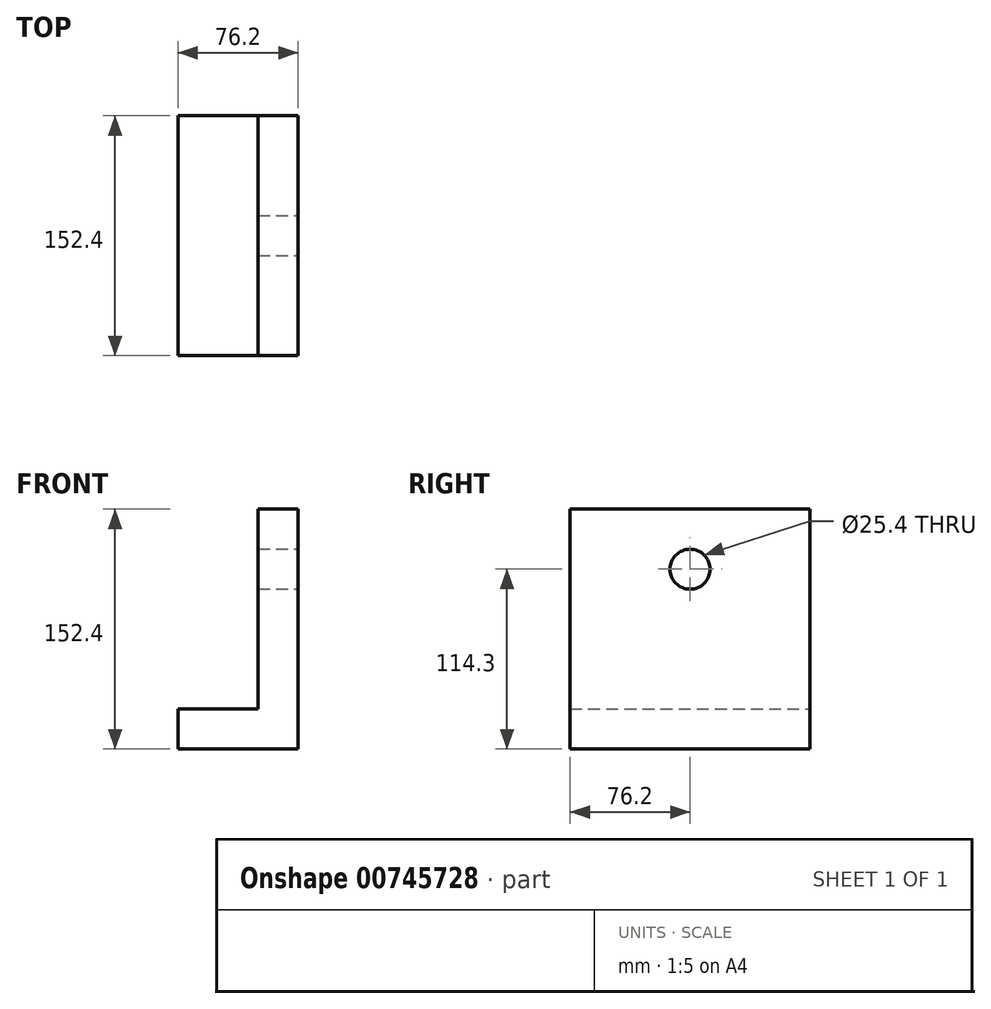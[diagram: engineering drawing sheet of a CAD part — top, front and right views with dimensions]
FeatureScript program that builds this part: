
annotation { "Feature Type Name" : "Feature", "Feature Type Description" : "" }
export const myFeature = defineFeature(function(context is Context, id is Id, definition is map)
    precondition{}
    {
        {
            var Q0;
            Q0=qCreatedBy(makeId("Front.planeOp"),FACE);
            var sketch = newSketch(context, id + "F0", { "sketchPlane" : qUnion([Q0])});
            skLineSegment(sketch, "E0", {"start": v(0, 0) * mm, "end": v(-76.2, 0) * mm});
            skLineSegment(sketch, "E1", {"start": v(-76.2, 0) * mm, "end": v(-76.2, 25.4) * mm});
            skLineSegment(sketch, "E2", {"start": v(-76.2, 25.4) * mm, "end": v(-25.4, 25.4) * mm});
            skLineSegment(sketch, "E3", {"start": v(-25.4, 25.4) * mm, "end": v(-25.4, 152.4) * mm});
            skLineSegment(sketch, "E4", {"start": v(-25.4, 152.4) * mm, "end": v(0, 152.4) * mm});
            skLineSegment(sketch, "E5", {"start": v(0, 152.4) * mm, "end": v(0, 0) * mm});
            skLineSegment(sketch, "E6", {"start": v(-25.4, 88.9) * mm, "end": v(0, 88.9) * mm});
            skPoint(sketch, "E6.endSnap0", {"position": v(-25.4, 88.9) * mm});
            skLineSegment(sketch, "E7", {"start": v(-50.8, 25.4) * mm, "end": v(-50.8, 0) * mm});
            skSolve(sketch);
        }
        {
            var Q0;
            Q0 = qSketchRegion(id + "F0", true);
            extrude(context, id + "F1", {"entities" : qUnion([Q0]), "endBound" : BoundingType.SYMMETRIC, "depth" : 152.4 * mm, "offsetDistance" : 25.4 * mm});
        }
        {
            var Q0;
            Q0=makeQuery(id+"F1.opExtrude","SWEPT_FACE",FACE,{"disambiguationData":[OSD([sQuery(id+"F0.wireOp",EDGE,"E5")])]});
            var sketch = newSketch(context, id + "F2", { "sketchPlane" : qUnion([Q0])});
            skCircle(sketch, "E8", {"center": v(0, 114.3) * mm, "radius": 12.7 * mm});
            skSolve(sketch);
        }
        {
            var Q0;
            Q0=makeQuery(id+"F2.imprint","IMPRINT",FACE,{"disambiguationData":[TD([[makeQuery(id+"F2.imprint","IMPRINT",EDGE,{"derivedFrom":sQuery(id+"F2.wireOp",EDGE,"E8")}),1.0]])]});
            extrude(context, id + "F3", {"entities" : qUnion([Q0]), "operationType" : NewBodyOperationType.REMOVE, "endBound" : BoundingType.THROUGH_ALL, "oppositeDirection" : true, "depth" : 25.4 * mm, "offsetDistance" : 25.4 * mm});
        }
    });
